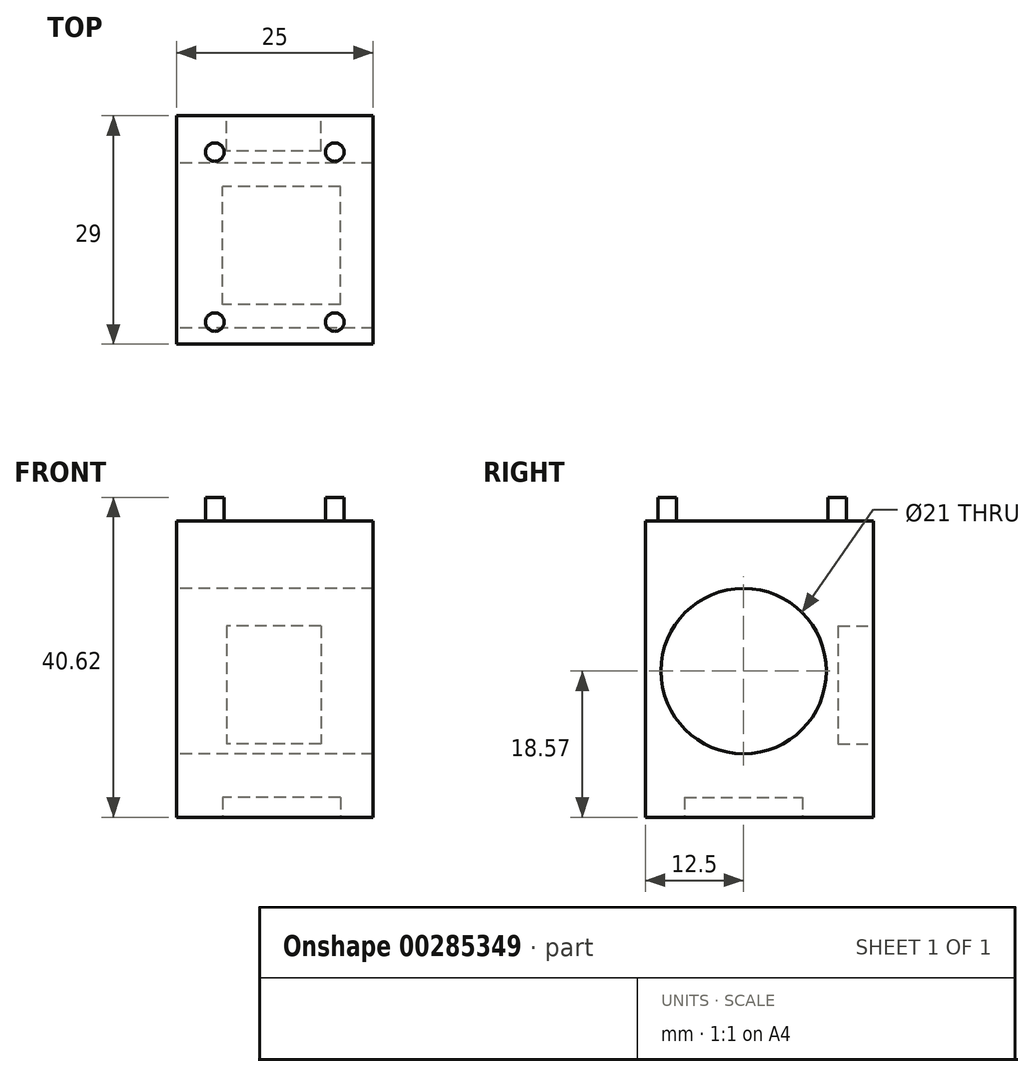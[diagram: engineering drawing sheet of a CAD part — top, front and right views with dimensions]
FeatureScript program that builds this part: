
annotation { "Feature Type Name" : "Feature", "Feature Type Description" : "" }
export const myFeature = defineFeature(function(context is Context, id is Id, definition is map)
    precondition{}
    {
        {
            var Q0;
            Q0=qCreatedBy(makeId("Right.planeOp"),FACE);
            var sketch = newSketch(context, id + "F0", { "sketchPlane" : qUnion([Q0])});
            skCircle(sketch, "E0", {"center": v(0, 0) * mm, "radius": 10.5 * mm});
            skLineSegment(sketch, "E1", {"start": v(16.5, 19.05) * mm, "end": v(-12.5, 19.05) * mm});
            skPoint(sketch, "E2", {"position": v(0, 19.05) * mm});
            skLineSegment(sketch, "E3", {"start": v(-1.89, -18.57) * mm, "end": v(-1.89, -17.96) * mm});
            skLineSegment(sketch, "E4", {"start": v(16.5, 19.05) * mm, "end": v(16.5, -18.57) * mm});
            skLineSegment(sketch, "E5", {"start": v(-12.5, 19.05) * mm, "end": v(-12.5, -18.57) * mm});
            skLineSegment(sketch, "E6", {"start": v(16.5, -18.57) * mm, "end": v(-12.5, -18.57) * mm});
            skLineSegment(sketch, "E7", {"start": v(-12.5, 0) * mm, "end": v(-10.5, 0) * mm});
            skLineSegment(sketch, "E8", {"start": v(10.5, 0) * mm, "end": v(16.5, 0) * mm});
            skSolve(sketch);
        }
        {
            var Q0;
            Q0=qSketchRegion(id+"F0",true);
            extrude(context, id + "F1", {"entities" : qUnion([Q0]), "endBound" : BoundingType.SYMMETRIC, "depth" : 25 * mm});
        }
        {
            var Q0;
            Q0=makeQuery(id+"F1.opExtrude","SWEPT_FACE",FACE,{"disambiguationData":[OSD([sQuery(id+"F0.wireOp",EDGE,"E1")])]});
            var sketch = newSketch(context, id + "F2", { "sketchPlane" : qUnion([Q0])});
            skLineSegment(sketch, "E9", {"start": v(-10.16, -9.72) * mm, "end": v(10.16, -9.72) * mm, "construction": true});
            skLineSegment(sketch, "E10", {"start": v(-7.62, -12.26) * mm, "end": v(-7.62, 14.41) * mm, "construction": true});
            skLineSegment(sketch, "E11", {"start": v(7.62, -12.26) * mm, "end": v(7.62, 14.41) * mm, "construction": true});
            skLineSegment(sketch, "E12", {"start": v(7.62, 14.41) * mm, "end": v(-7.62, -12.26) * mm, "construction": true});
            skPoint(sketch, "E13", {"position": v(0, 1.08) * mm});
            skCircle(sketch, "E14", {"center": v(-7.62, -9.72) * mm, "radius": 1.18 * mm});
            skCircle(sketch, "E15", {"center": v(7.62, -9.72) * mm, "radius": 1.18 * mm});
            skLineSegment(sketch, "E16", {"start": v(-10.16, 1.08) * mm, "end": v(10.16, 1.08) * mm, "construction": true});
            skCircle(sketch, "E17.MirrorC", {"center": v(7.62, 11.87) * mm, "radius": 1.18 * mm});
            skCircle(sketch, "E18.MirrorC", {"center": v(-7.62, 11.87) * mm, "radius": 1.18 * mm});
            skLineSegment(sketch, "E19", {"start": v(7.62, 11.87) * mm, "end": v(7.62, -9.72) * mm});
            skLineSegment(sketch, "E20", {"start": v(12.5, 16.5) * mm, "end": v(12.5, -12.5) * mm});
            skSolve(sketch);
        }
        {
            var Q0;
            Q0 = qSketchRegion(id + "F2", true);
            extrude(context, id + "F3", {"entities" : qUnion([Q0]), "operationType" : NewBodyOperationType.ADD, "depth" : 3 * mm});
        }
        {
            var Q0;
            Q0=makeQuery(id+"F1.opExtrude","SWEPT_FACE",FACE,{"disambiguationData":[OSD([sQuery(id+"F0.wireOp",EDGE,"E6")])]});
            var sketch = newSketch(context, id + "F4", { "sketchPlane" : qUnion([Q0])});
            skLineSegment(sketch, "E21.bottom", {"start": v(8.34, 7.5) * mm, "end": v(-6.66, 7.5) * mm});
            skLineSegment(sketch, "E21.top", {"start": v(8.34, -7.5) * mm, "end": v(-6.66, -7.5) * mm});
            skLineSegment(sketch, "E21.left", {"start": v(8.34, 7.5) * mm, "end": v(8.34, -7.5) * mm});
            skLineSegment(sketch, "E21.right", {"start": v(-6.66, 7.5) * mm, "end": v(-6.66, -7.5) * mm});
            skSolve(sketch);
        }
        {
            var Q0;
            Q0 = qSketchRegion(id + "F4", true);
            extrude(context, id + "F5", {"entities" : qUnion([Q0]), "operationType" : NewBodyOperationType.REMOVE, "oppositeDirection" : true, "depth" : 2.5 * mm});
        }
        {
            var Q0;
            Q0=makeQuery(id+"F1.opExtrude","SWEPT_FACE",FACE,{"disambiguationData":[OSD([sQuery(id+"F0.wireOp",EDGE,"E4")])]});
            var sketch = newSketch(context, id + "F6", { "sketchPlane" : qUnion([Q0])});
            skLineSegment(sketch, "E22.bottom", {"start": v(-5.87, 5.72) * mm, "end": v(6.13, 5.72) * mm});
            skLineSegment(sketch, "E22.top", {"start": v(-5.87, -9.28) * mm, "end": v(6.13, -9.28) * mm});
            skLineSegment(sketch, "E22.left", {"start": v(-5.87, 5.72) * mm, "end": v(-5.87, -9.28) * mm});
            skLineSegment(sketch, "E22.right", {"start": v(6.13, 5.72) * mm, "end": v(6.13, -9.28) * mm});
            skSolve(sketch);
        }
        {
            var Q0;
            Q0 = qSketchRegion(id + "F6", true);
            extrude(context, id + "F7", {"entities" : qUnion([Q0]), "operationType" : NewBodyOperationType.REMOVE, "oppositeDirection" : true, "depth" : 4.5 * mm});
        }
    });
